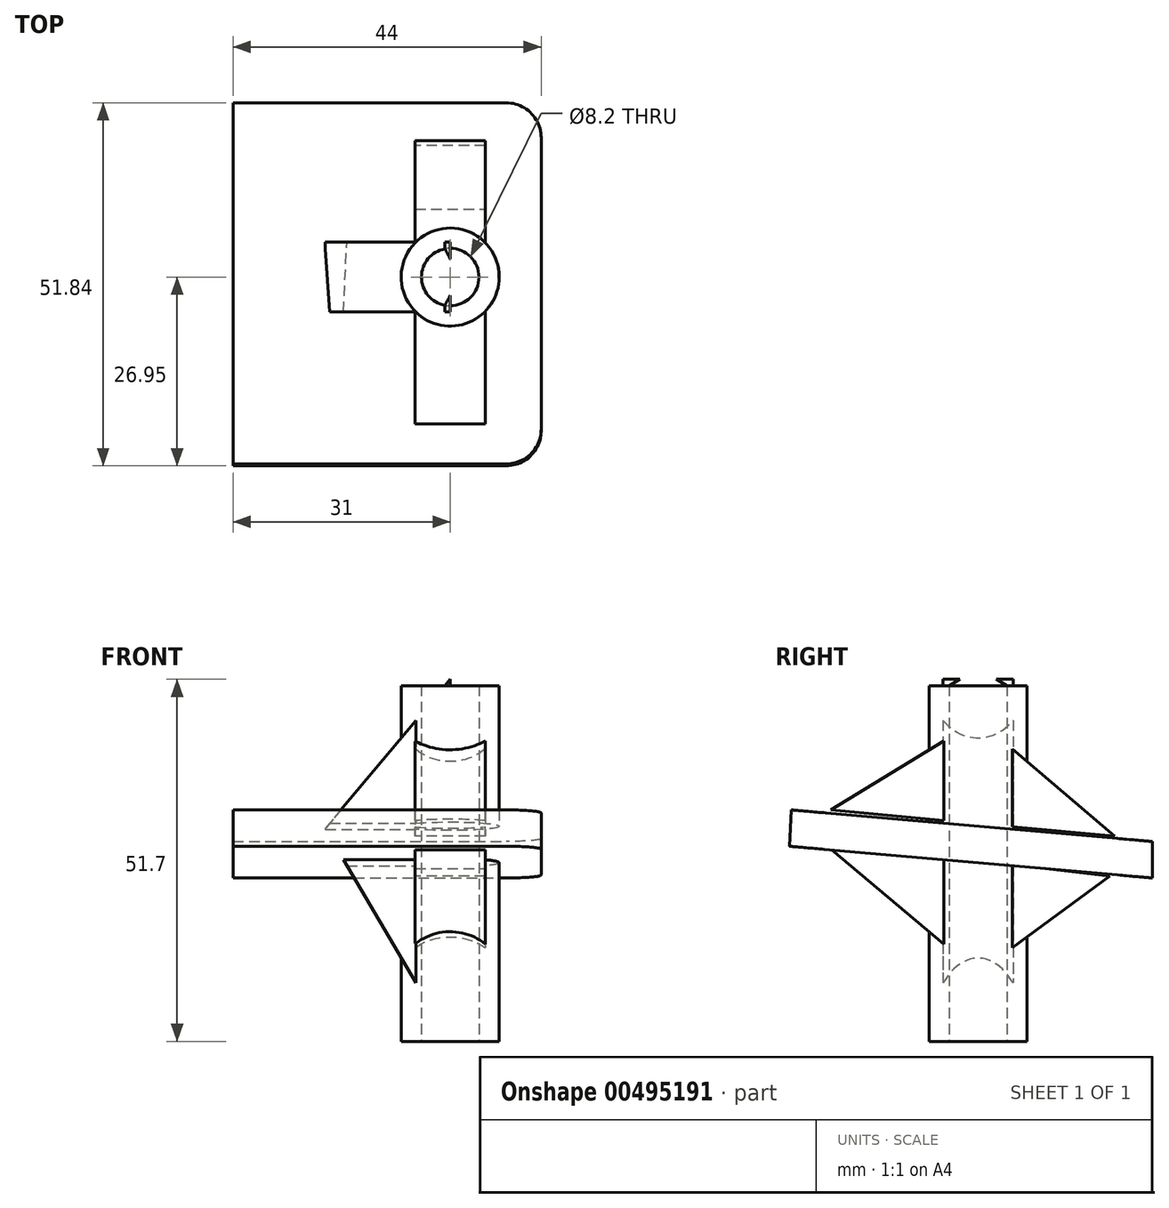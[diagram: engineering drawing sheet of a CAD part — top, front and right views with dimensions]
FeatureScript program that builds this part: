
annotation { "Feature Type Name" : "Feature", "Feature Type Description" : "" }
export const myFeature = defineFeature(function(context is Context, id is Id, definition is map)
    precondition{}
    {
        {
            var Q0;
            Q0=qCreatedBy(makeId("Top.planeOp"),FACE);
            var sketch = newSketch(context, id + "F0", { "sketchPlane" : qUnion([Q0])});
            skCircle(sketch, "E0", {"center": v(0, 0) * mm, "radius": 4.1 * mm});
            skCircle(sketch, "E1", {"center": v(0, 0) * mm, "radius": 7 * mm});
            skSolve(sketch);
        }
        {
            var Q0;
            Q0=makeQuery(id+"F0.imprint","IMPRINT",FACE,{"disambiguationData":[TD([[makeQuery(id+"F0.imprint","IMPRINT",EDGE,{"derivedFrom":sQuery(id+"F0.wireOp",EDGE,"E0")}),-1.0]])]});
            extrude(context, id + "F1", {"entities" : qUnion([Q0]), "depth" : 50.8 * mm});
        }
        {
            var Q0;
            Q0=qCreatedBy(makeId("Right.planeOp"),FACE);
            var sketch = newSketch(context, id + "F2", { "sketchPlane" : qUnion([Q0])});
            skLineSegment(sketch, "E2", {"start": v(24.9, 23.33) * mm, "end": v(-65.27, 23.33) * mm});
            skLineSegment(sketch, "E3", {"start": v(0, 0) * mm, "end": v(0, 82.8) * mm});
            skLineSegment(sketch, "E4", {"start": v(24.9, 23.33) * mm, "end": v(-26.95, 27.86) * mm});
            skLineSegment(sketch, "E5", {"start": v(24.89, 28.54) * mm, "end": v(-26.7, 33.06) * mm});
            skLineSegment(sketch, "E6", {"start": v(-26.7, 33.06) * mm, "end": v(-26.95, 27.86) * mm});
            skLineSegment(sketch, "E7", {"start": v(24.9, 23.33) * mm, "end": v(24.89, 28.54) * mm});
            skSolve(sketch);
        }
        {
            var Q0;
            {var subQ5=sQuery(id+"F2.wireOp",EDGE,"E7");Q0=makeQuery(id+"F2.imprint","IMPRINT",FACE,{"disambiguationData":[TD([[makeQuery(id+"F2.imprint","IMPRINT",EDGE,{"derivedFrom":subQ5}),1.0]])]});}
            var Q1;
            {var subQ5=sQuery(id+"F2.wireOp",EDGE,"E6");Q1=makeQuery(id+"F2.imprint","IMPRINT",FACE,{"disambiguationData":[TD([[makeQuery(id+"F2.imprint","IMPRINT",EDGE,{"derivedFrom":subQ5}),1.0]])]});}
            extrude(context, id + "F3", {"entities" : qUnion([Q0, Q1]), "operationType" : NewBodyOperationType.ADD, "oppositeDirection" : true, "depth" : 31 * mm, "hasSecondDirection" : true, "secondDirectionOppositeDirection" : false, "secondDirectionDepth" : 13 * mm});
        }
        {
            var Q0;
            Q0=sQuery(id+"F0.wireOp",VERTEX,"E1.center");
            var Q1;
            Q1=makeQuery(id+"F1.opExtrude","SWEPT_BODY",BODY,{"disambiguationData":[OSD([sQuery(id+"F0.wireOp",EDGE,"E0"),sQuery(id+"F0.wireOp",EDGE,"E1")])]});
            hole(context, id + "F4", {"style" : HoleStyle.SIMPLE, "endStyle" : HoleEndStyle.BLIND, "oppositeDirection" : true, "holeDiameter" : 8 * mm, "holeDepth" : 50.8 * mm, "isTappedThrough" : true, "tappedDepth" : 12.7 * mm, "tapClearance" : 3, "startFromSketch" : true, "locations" : qUnion([Q0]), "scope" : qUnion([Q1])});
        }
        {
            var Q0;
            Q0=makeQuery(id+"F3.opExtrude","CAP_EDGE",EDGE,{"disambiguationData":[OSD([sQuery(id+"F2.wireOp",EDGE,"E7")])],"isStart":true});
            var Q1;
            Q1=makeQuery(id+"F3.opExtrude","CAP_EDGE",EDGE,{"disambiguationData":[OSD([sQuery(id+"F2.wireOp",EDGE,"E6")])],"isStart":true});
            fillet(context, id + "F5", {"entities" : qUnion([Q0, Q1]), "radius" : 5 * mm, "tangentPropagation" : true, "allowEdgeOverflow" : false});
        }
        {
            var Q0;
            Q0=qCreatedBy(makeId("Right.planeOp"),FACE);
            var sketch = newSketch(context, id + "F6", { "sketchPlane" : qUnion([Q0])});
            skPoint(sketch, "E8", {"position": v(18.79, 23.57) * mm});
            skPoint(sketch, "E9", {"position": v(-21.44, 27.78) * mm});
            skPoint(sketch, "E10", {"position": v(0, 9.79) * mm});
            skPoint(sketch, "E11", {"position": v(0, 25.81) * mm});
            skLineSegment(sketch, "E12", {"start": v(18.79, 23.57) * mm, "end": v(0, 9.79) * mm});
            skLineSegment(sketch, "E13", {"start": v(-21.44, 27.78) * mm, "end": v(0, 9.79) * mm});
            skLineSegment(sketch, "E14", {"start": v(18.79, 23.57) * mm, "end": v(0, 25.81) * mm});
            skLineSegment(sketch, "E15", {"start": v(-21.44, 27.78) * mm, "end": v(0, 25.81) * mm});
            skPoint(sketch, "E16", {"position": v(0, 31.06) * mm});
            skPoint(sketch, "E17", {"position": v(-21, 33.03) * mm});
            skPoint(sketch, "E18", {"position": v(19.47, 29.31) * mm});
            skLineSegment(sketch, "E19", {"start": v(0, 31.06) * mm, "end": v(-21, 33.03) * mm});
            skLineSegment(sketch, "E20", {"start": v(19.47, 29.31) * mm, "end": v(0, 31.06) * mm});
            skPoint(sketch, "E21", {"position": v(0, 45.94) * mm});
            skLineSegment(sketch, "E22", {"start": v(0, 45.94) * mm, "end": v(-21, 33.03) * mm});
            skLineSegment(sketch, "E23", {"start": v(0, 45.94) * mm, "end": v(19.47, 29.31) * mm});
            skSolve(sketch);
        }
        {
            var Q0;
            Q0=makeQuery(id+"F6.imprint","IMPRINT",FACE,{"disambiguationData":[TD([[makeQuery(id+"F6.imprint","IMPRINT",EDGE,{"derivedFrom":sQuery(id+"F6.wireOp",EDGE,"E12")}),-1.0]])]});
            var Q1;
            Q1=makeQuery(id+"F6.imprint","IMPRINT",FACE,{"disambiguationData":[TD([[makeQuery(id+"F6.imprint","IMPRINT",EDGE,{"derivedFrom":sQuery(id+"F6.wireOp",EDGE,"E19")}),-1.0]])]});
            extrude(context, id + "F7", {"entities" : qUnion([Q0, Q1]), "operationType" : NewBodyOperationType.ADD, "endBound" : BoundingType.SYMMETRIC, "depth" : 10 * mm});
        }
        {
            var Q0;
            Q0=qCreatedBy(makeId("Front.planeOp"),FACE);
            var sketch = newSketch(context, id + "F8", { "sketchPlane" : qUnion([Q0])});
            skPoint(sketch, "E24", {"position": v(-17.87, 30.37) * mm});
            skLineSegment(sketch, "E25", {"start": v(-17.87, 30.37) * mm, "end": v(0, 0) * mm});
            skPoint(sketch, "E26", {"position": v(0, 51.7) * mm});
            skLineSegment(sketch, "E27", {"start": v(0, 51.7) * mm, "end": v(-17.87, 30.37) * mm});
            skLineSegment(sketch, "E28", {"start": v(0, 0) * mm, "end": v(0, 51.7) * mm});
            skSolve(sketch);
        }
        {
            var Q0;
            Q0=makeQuery(id+"F8.imprint","IMPRINT",FACE,{"disambiguationData":[TD([[makeQuery(id+"F8.imprint","IMPRINT",EDGE,{"derivedFrom":sQuery(id+"F8.wireOp",EDGE,"E25")}),1.0]])]});
            extrude(context, id + "F9", {"entities" : qUnion([Q0]), "operationType" : NewBodyOperationType.ADD, "endBound" : BoundingType.SYMMETRIC, "depth" : 10 * mm});
        }
        {
            var Q0;
            Q0=sQuery(id+"F0.wireOp",VERTEX,"E0.center");
            var Q1;
            Q1=makeQuery(id+"F1.opExtrude","SWEPT_BODY",BODY,{"disambiguationData":[OSD([sQuery(id+"F0.wireOp",EDGE,"E0"),sQuery(id+"F0.wireOp",EDGE,"E1")])]});
            hole(context, id + "F10", {"style" : HoleStyle.SIMPLE, "endStyle" : HoleEndStyle.BLIND, "oppositeDirection" : true, "holeDiameter" : 8.2 * mm, "holeDepth" : 50.8 * mm, "isTappedThrough" : true, "tappedDepth" : 12.7 * mm, "tapClearance" : 3, "startFromSketch" : true, "locations" : qUnion([Q0]), "scope" : qUnion([Q1])});
        }
    });
